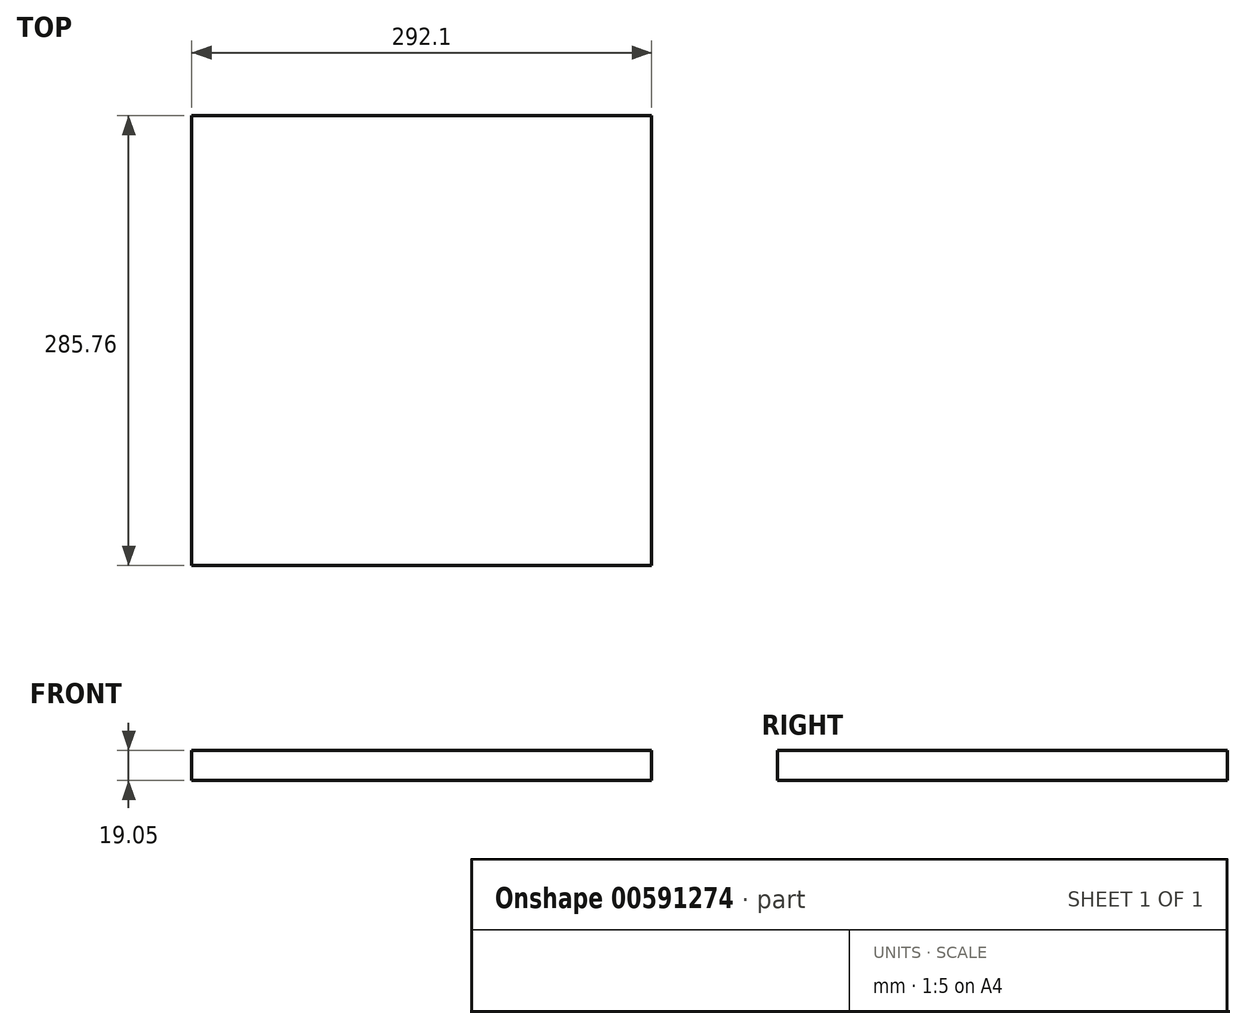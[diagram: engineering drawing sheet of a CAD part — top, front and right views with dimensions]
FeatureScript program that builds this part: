
annotation { "Feature Type Name" : "Feature", "Feature Type Description" : "" }
export const myFeature = defineFeature(function(context is Context, id is Id, definition is map)
    precondition{}
    {
        {
            var Q0;
            Q0=qCreatedBy(makeId("Top.planeOp"),FACE);
            var sketch = newSketch(context, id + "F0", { "sketchPlane" : qUnion([Q0])});
            skLineSegment(sketch, "E0.bottom", {"start": v(146.05, -142.87) * mm, "end": v(-146.05, -142.88) * mm});
            skLineSegment(sketch, "E0.top", {"start": v(146.05, 142.88) * mm, "end": v(-146.05, 142.88) * mm});
            skLineSegment(sketch, "E0.left", {"start": v(146.05, -142.87) * mm, "end": v(146.05, 142.88) * mm});
            skLineSegment(sketch, "E0.right", {"start": v(-146.05, -142.88) * mm, "end": v(-146.05, 142.88) * mm});
            skPoint(sketch, "E0.middle", {"position": v(0, 0) * mm});
            skSolve(sketch);
        }
        {
            var Q0;
            Q0 = qSketchRegion(id + "F0", true);
            extrude(context, id + "F1", {"entities" : qUnion([Q0]), "depth" : 19.05 * mm, "offsetDistance" : 25.4 * mm});
        }
    });
